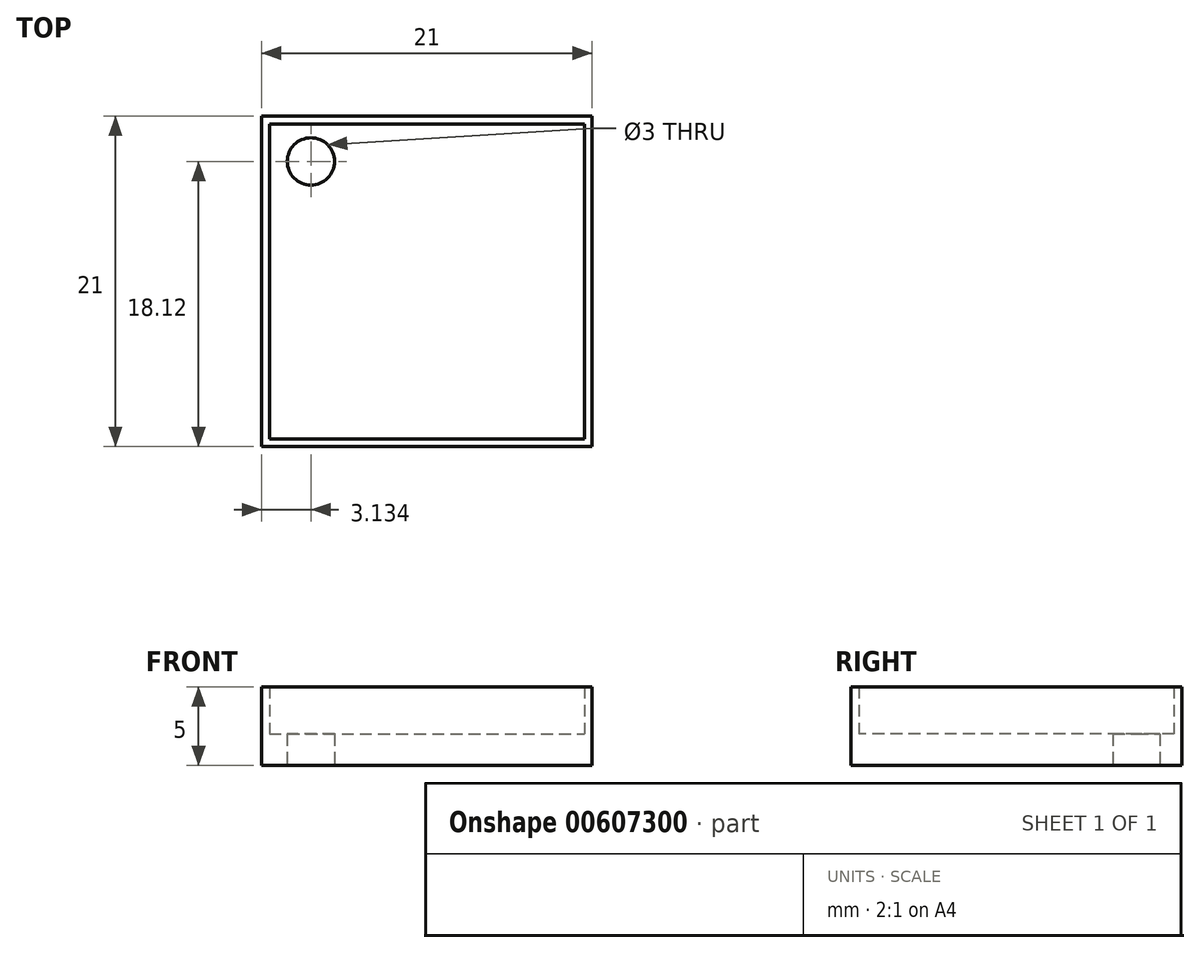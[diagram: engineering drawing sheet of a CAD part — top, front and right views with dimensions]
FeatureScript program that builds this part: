
annotation { "Feature Type Name" : "Feature", "Feature Type Description" : "" }
export const myFeature = defineFeature(function(context is Context, id is Id, definition is map)
    precondition{}
    {
        {
            var Q0;
            Q0=qCreatedBy(makeId("Top.planeOp"),FACE);
            var sketch = newSketch(context, id + "F0", { "sketchPlane" : qUnion([Q0])});
            skLineSegment(sketch, "E0.bottom", {"start": v(-10, 10) * mm, "end": v(10, 10) * mm});
            skLineSegment(sketch, "E0.top", {"start": v(-10, -10) * mm, "end": v(10, -10) * mm});
            skLineSegment(sketch, "E0.left", {"start": v(-10, 10) * mm, "end": v(-10, -10) * mm});
            skLineSegment(sketch, "E0.right", {"start": v(10, 10) * mm, "end": v(10, -10) * mm});
            skPoint(sketch, "E0.middle", {"position": v(0, 0) * mm});
            skLineSegment(sketch, "E1.bottom", {"start": v(-10.5, 10.5) * mm, "end": v(10.5, 10.5) * mm});
            skLineSegment(sketch, "E1.top", {"start": v(-10.5, -10.5) * mm, "end": v(10.5, -10.5) * mm});
            skLineSegment(sketch, "E1.left", {"start": v(-10.5, 10.5) * mm, "end": v(-10.5, -10.5) * mm});
            skLineSegment(sketch, "E1.right", {"start": v(10.5, 10.5) * mm, "end": v(10.5, -10.5) * mm});
            skSolve(sketch);
        }
        {
            var Q0;
            Q0 = qSketchRegion(id + "F0", true);
            extrude(context, id + "F1", {"entities" : qUnion([Q0]), "depth" : 5 * mm, "offsetDistance" : 25 * mm});
        }
        {
            var Q0;
            Q0=qCreatedBy(makeId("Top.planeOp"),FACE);
            var sketch = newSketch(context, id + "F2", { "sketchPlane" : qUnion([Q0])});
            skLineSegment(sketch, "E2.bottom", {"start": v(-10.5, 10.5) * mm, "end": v(10.5, 10.5) * mm});
            skLineSegment(sketch, "E2.top", {"start": v(-10.5, -10.5) * mm, "end": v(10.5, -10.5) * mm});
            skLineSegment(sketch, "E2.left", {"start": v(-10.5, 10.5) * mm, "end": v(-10.5, -10.5) * mm});
            skLineSegment(sketch, "E2.right", {"start": v(10.5, 10.5) * mm, "end": v(10.5, -10.5) * mm});
            skPoint(sketch, "E2.middle", {"position": v(0, 0) * mm});
            skCircle(sketch, "E3", {"center": v(-7.37, 7.62) * mm, "radius": 1.5 * mm});
            skSolve(sketch);
        }
        {
            var Q0;
            Q0=makeQuery(id+"F2.imprint","IMPRINT",FACE,{"disambiguationData":[TD([[makeQuery(id+"F2.imprint","IMPRINT",EDGE,{"derivedFrom":sQuery(id+"F2.wireOp",EDGE,"E2.bottom")}),-1.0]])]});
            extrude(context, id + "F3", {"entities" : qUnion([Q0]), "operationType" : NewBodyOperationType.ADD, "depth" : 2 * mm, "offsetDistance" : 25 * mm});
        }
    });
